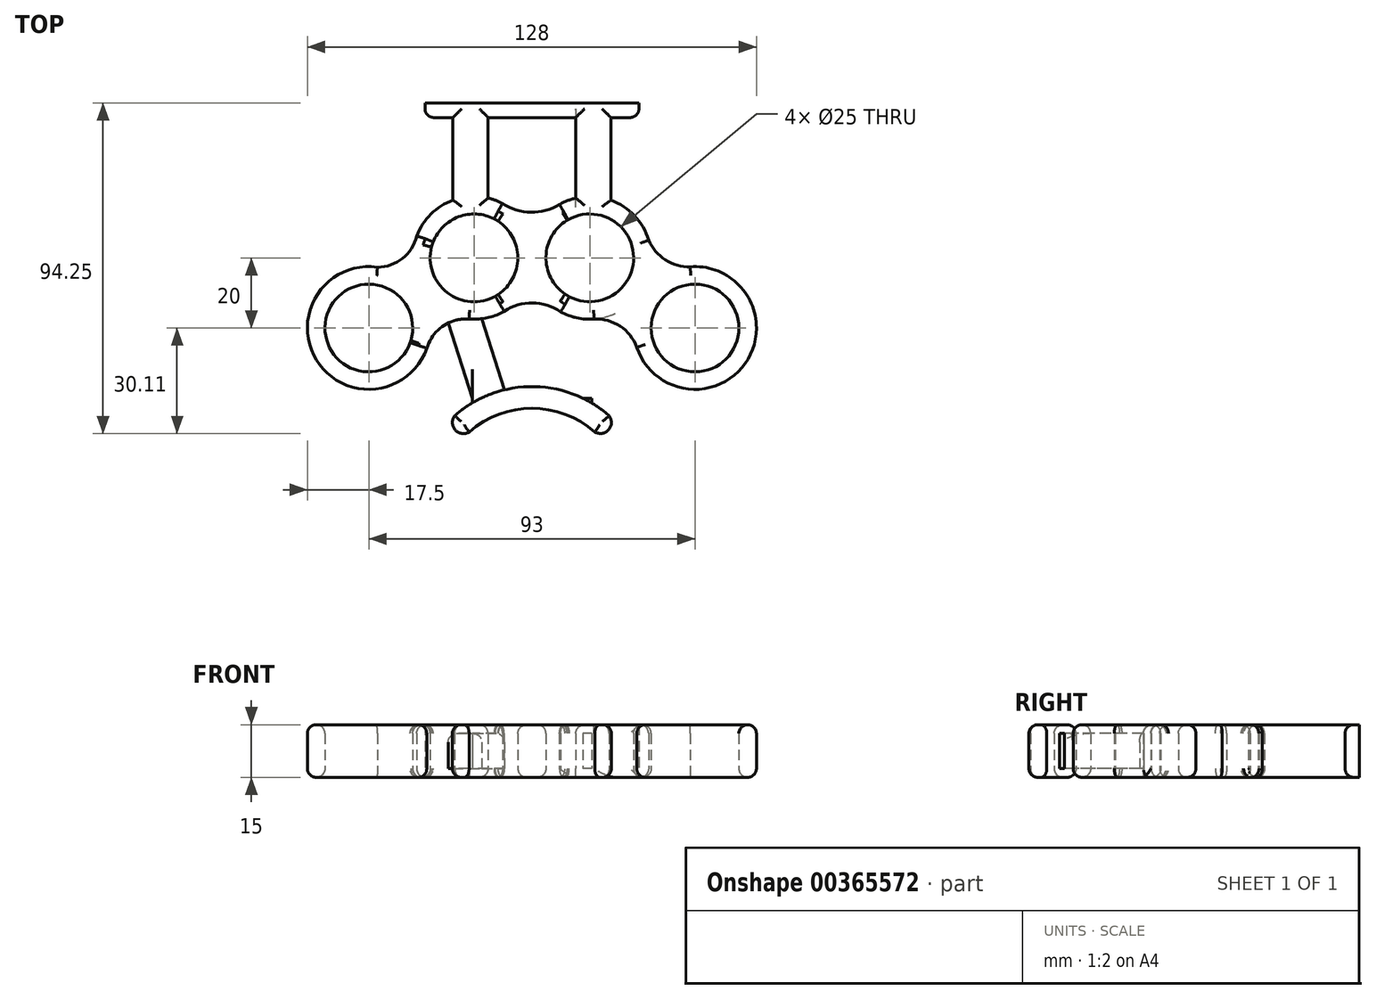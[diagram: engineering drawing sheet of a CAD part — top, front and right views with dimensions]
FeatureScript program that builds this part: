
annotation { "Feature Type Name" : "Feature", "Feature Type Description" : "" }
export const myFeature = defineFeature(function(context is Context, id is Id, definition is map)
    precondition{}
    {
        {
            var Q0;
            Q0=qCreatedBy(makeId("Top.planeOp"),FACE);
            var sketch = newSketch(context, id + "F0", { "sketchPlane" : qUnion([Q0])});
            skLineSegment(sketch, "E0", {"start": v(0, 0) * mm, "end": v(-16.5, 0) * mm});
            skLineSegment(sketch, "E1", {"start": v(0, 0) * mm, "end": v(16.5, 0) * mm});
            skCircle(sketch, "E2", {"center": v(-16.5, 0) * mm, "radius": 12.5 * mm});
            skCircle(sketch, "E3", {"center": v(16.5, 0) * mm, "radius": 12.5 * mm});
            skCircle(sketch, "E4", {"center": v(-46.5, -20) * mm, "radius": 12.5 * mm});
            skCircle(sketch, "E5", {"center": v(46.5, -20) * mm, "radius": 12.5 * mm});
            skCircle(sketch, "E6.0", {"center": v(-46.5, -20) * mm, "radius": 17.5 * mm});
            skCircle(sketch, "E7.0", {"center": v(-16.5, 0) * mm, "radius": 17.5 * mm});
            skCircle(sketch, "E8.0", {"center": v(16.5, 0) * mm, "radius": 17.5 * mm});
            skCircle(sketch, "E9.0", {"center": v(46.5, -20) * mm, "radius": 17.5 * mm});
            skArc(sketch, "E10", {"start": v(-8.38, 15.5) * mm, "mid": v(-0.3, 13.01) * mm, "end": v(7.85, 15.21) * mm});
            skArc(sketch, "E11", {"start": v(-44.04, -2.67) * mm, "mid": v(-36.9, -0.16) * mm, "end": v(-32.85, 6.23) * mm});
            skArc(sketch, "E12", {"start": v(8.17, -15.4) * mm, "mid": v(0.16, -12.86) * mm, "end": v(-7.9, -15.24) * mm});
            skArc(sketch, "E13", {"start": v(33.26, 5.03) * mm, "mid": v(38.06, -0.54) * mm, "end": v(45.14, -2.55) * mm});
            skArc(sketch, "E14", {"start": v(-17.95, -17.44) * mm, "mid": v(-25.43, -19.49) * mm, "end": v(-29.98, -25.76) * mm});
            skArc(sketch, "E15", {"start": v(29.9, -25.53) * mm, "mid": v(25.15, -19.48) * mm, "end": v(17.73, -17.46) * mm});
            skLineSegment(sketch, "E16", {"start": v(-16.5, 0) * mm, "end": v(-46.5, -20) * mm});
            skLineSegment(sketch, "E17", {"start": v(16.5, 0) * mm, "end": v(46.5, -20) * mm});
            skSolve(sketch);
        }
        {
            var Q0;
            {var subQ4=sQuery(id+"F0.wireOp",EDGE,"E7.0");var subQ5=sQuery(id+"F0.wireOp",EDGE,"E1");var subQ6=makeQuery(id+"F0.imprint","INTERSECT",VERTEX,{"derivedFrom":[subQ5,subQ4]});Q0=makeQuery(id+"F0.imprint","IMPRINT",FACE,{"disambiguationData":[TD([[makeQuery(id+"F0.imprint","IMPRINT",EDGE,{"disambiguationData":[TD([[subQ6,-1.0]])],"derivedFrom":subQ5}),1.0]])]});}
            var Q1;
            {var subQ0=sQuery(id+"F0.wireOp",EDGE,"E1");var subQ1=sQuery(id+"F0.wireOp",EDGE,"E0");var subQ2=makeQuery(id+"F0.imprint","INTERSECT",VERTEX,{"derivedFrom":[subQ1,subQ0]});Q1=makeQuery(id+"F0.imprint","IMPRINT",FACE,{"disambiguationData":[TD([[makeQuery(id+"F0.imprint","IMPRINT",EDGE,{"disambiguationData":[TD([[subQ2,-1.0]])],"derivedFrom":subQ1}),-1.0]])]});}
            var Q2;
            {var subQ0=sQuery(id+"F0.wireOp",EDGE,"E10");var subQ1=sQuery(id+"F0.wireOp",EDGE,"E7.0");var subQ2=makeQuery(id+"F0.imprint","INTERSECT",VERTEX,{"disambiguationData":[OD(1.0)],"derivedFrom":[subQ1,subQ0]});Q2=makeQuery(id+"F0.imprint","IMPRINT",FACE,{"disambiguationData":[TD([[makeQuery(id+"F0.imprint","IMPRINT",EDGE,{"disambiguationData":[TD([[subQ2,1.0]])],"derivedFrom":subQ1}),-1.0]])]});}
            var Q3;
            {var subQ5=sQuery(id+"F0.wireOp",EDGE,"E8.0");var subQ6=sQuery(id+"F0.wireOp",EDGE,"E0");var subQ7=makeQuery(id+"F0.imprint","INTERSECT",VERTEX,{"derivedFrom":[subQ6,subQ5]});Q3=makeQuery(id+"F0.imprint","IMPRINT",FACE,{"disambiguationData":[TD([[makeQuery(id+"F0.imprint","IMPRINT",EDGE,{"disambiguationData":[TD([[subQ7,-1.0]])],"derivedFrom":subQ6}),-1.0]])]});}
            var Q4;
            {var subQ4=sQuery(id+"F0.wireOp",EDGE,"E8.0");var subQ5=sQuery(id+"F0.wireOp",EDGE,"E0");var subQ6=makeQuery(id+"F0.imprint","INTERSECT",VERTEX,{"derivedFrom":[subQ5,subQ4]});Q4=makeQuery(id+"F0.imprint","IMPRINT",FACE,{"disambiguationData":[TD([[makeQuery(id+"F0.imprint","IMPRINT",EDGE,{"disambiguationData":[TD([[subQ6,-1.0]])],"derivedFrom":subQ5}),1.0]])]});}
            var Q5;
            {var subQ3=sQuery(id+"F0.wireOp",EDGE,"E7.0");var subQ5=sQuery(id+"F0.wireOp",EDGE,"E1");var subQ6=makeQuery(id+"F0.imprint","INTERSECT",VERTEX,{"derivedFrom":[subQ5,subQ3]});Q5=makeQuery(id+"F0.imprint","IMPRINT",FACE,{"disambiguationData":[TD([[makeQuery(id+"F0.imprint","IMPRINT",EDGE,{"disambiguationData":[TD([[subQ6,-1.0]])],"derivedFrom":subQ5}),-1.0]])]});}
            var Q6;
            {var subQ0=sQuery(id+"F0.wireOp",EDGE,"E1");var subQ1=sQuery(id+"F0.wireOp",EDGE,"E0");var subQ2=makeQuery(id+"F0.imprint","INTERSECT",VERTEX,{"derivedFrom":[subQ1,subQ0]});Q6=makeQuery(id+"F0.imprint","IMPRINT",FACE,{"disambiguationData":[TD([[makeQuery(id+"F0.imprint","IMPRINT",EDGE,{"disambiguationData":[TD([[subQ2,-1.0]])],"derivedFrom":subQ1}),1.0]])]});}
            var Q7;
            {var subQ0=sQuery(id+"F0.wireOp",EDGE,"E12");var subQ1=sQuery(id+"F0.wireOp",EDGE,"E7.0");var subQ2=makeQuery(id+"F0.imprint","INTERSECT",VERTEX,{"disambiguationData":[OD(1.0)],"derivedFrom":[subQ1,subQ0]});Q7=makeQuery(id+"F0.imprint","IMPRINT",FACE,{"disambiguationData":[TD([[makeQuery(id+"F0.imprint","IMPRINT",EDGE,{"disambiguationData":[TD([[subQ2,-1.0]])],"derivedFrom":subQ1}),-1.0]])]});}
            var Q8;
            {var subQ0=sQuery(id+"F0.wireOp",EDGE,"E15");Q8=makeQuery(id+"F0.imprint","IMPRINT",FACE,{"disambiguationData":[TD([[makeQuery(id+"F0.imprint","IMPRINT",EDGE,{"derivedFrom":subQ0}),-1.0]])]});}
            var Q9;
            {var subQ0=sQuery(id+"F0.wireOp",EDGE,"E13");Q9=makeQuery(id+"F0.imprint","IMPRINT",FACE,{"disambiguationData":[TD([[makeQuery(id+"F0.imprint","IMPRINT",EDGE,{"derivedFrom":subQ0}),-1.0]])]});}
            var Q10;
            Q10=makeQuery(id+"F0.imprint","IMPRINT",FACE,{"disambiguationData":[TD([[makeQuery(id+"F0.imprint","IMPRINT",EDGE,{"derivedFrom":sQuery(id+"F0.wireOp",EDGE,"E5")}),-1.0]])]});
            var Q11;
            Q11=makeQuery(id+"F0.imprint","IMPRINT",FACE,{"disambiguationData":[TD([[makeQuery(id+"F0.imprint","IMPRINT",EDGE,{"derivedFrom":sQuery(id+"F0.wireOp",EDGE,"E4")}),-1.0]])]});
            var Q12;
            {var subQ0=sQuery(id+"F0.wireOp",EDGE,"E16");var subQ1=sQuery(id+"F0.wireOp",EDGE,"E6.0");var subQ2=makeQuery(id+"F0.imprint","INTERSECT",VERTEX,{"derivedFrom":[subQ1,subQ0]});Q12=makeQuery(id+"F0.imprint","IMPRINT",FACE,{"disambiguationData":[TD([[makeQuery(id+"F0.imprint","IMPRINT",EDGE,{"disambiguationData":[TD([[subQ2,1.0]])],"derivedFrom":subQ1}),-1.0]])]});}
            var Q13;
            {var subQ0=sQuery(id+"F0.wireOp",EDGE,"E11");var subQ1=sQuery(id+"F0.wireOp",EDGE,"E6.0");var subQ2=makeQuery(id+"F0.imprint","INTERSECT",VERTEX,{"derivedFrom":[subQ1,subQ0]});Q13=makeQuery(id+"F0.imprint","IMPRINT",FACE,{"disambiguationData":[TD([[makeQuery(id+"F0.imprint","IMPRINT",EDGE,{"disambiguationData":[TD([[subQ2,1.0]])],"derivedFrom":subQ1}),-1.0]])]});}
            extrude(context, id + "F1", {"entities" : qUnion([Q0, Q1, Q2, Q3, Q4, Q5, Q6, Q7, Q8, Q9, Q10, Q11, Q12, Q13]), "depth" : 15 * mm});
        }
        {
            var Q0;
            Q0=qCreatedBy(makeId("Top.planeOp"),FACE);
            var sketch = newSketch(context, id + "F2", { "sketchPlane" : qUnion([Q0])});
            skLineSegment(sketch, "E18", {"start": v(0, 0) * mm, "end": v(0, 15) * mm});
            skLineSegment(sketch, "E19", {"start": v(0, 15) * mm, "end": v(-12.5, 15) * mm});
            skLineSegment(sketch, "E20", {"start": v(0, 15) * mm, "end": v(12.5, 15) * mm});
            skLineSegment(sketch, "E21", {"start": v(-12.5, 15) * mm, "end": v(-12.5, 40) * mm});
            skLineSegment(sketch, "E22", {"start": v(12.5, 15) * mm, "end": v(12.5, 40) * mm});
            skLineSegment(sketch, "E23", {"start": v(12.5, 15) * mm, "end": v(22.5, 15) * mm});
            skLineSegment(sketch, "E24", {"start": v(22.5, 15) * mm, "end": v(22.5, 40) * mm});
            skLineSegment(sketch, "E25", {"start": v(-12.5, 15) * mm, "end": v(-22.5, 15) * mm});
            skLineSegment(sketch, "E26", {"start": v(-22.5, 15) * mm, "end": v(-22.5, 40) * mm});
            skLineSegment(sketch, "E27", {"start": v(-22.5, 40) * mm, "end": v(-12.5, 40) * mm});
            skLineSegment(sketch, "E28", {"start": v(12.5, 40) * mm, "end": v(22.5, 40) * mm});
            skLineSegment(sketch, "E29", {"start": v(30.5, 40) * mm, "end": v(30.5, 44.14) * mm});
            skLineSegment(sketch, "E30", {"start": v(30.5, 44.14) * mm, "end": v(-30.5, 44.14) * mm});
            skLineSegment(sketch, "E31", {"start": v(-30.5, 44.14) * mm, "end": v(-30.5, 40) * mm});
            skLineSegment(sketch, "E32", {"start": v(-30.5, 40) * mm, "end": v(-22.5, 40) * mm});
            skLineSegment(sketch, "E33", {"start": v(-12.5, 40) * mm, "end": v(12.5, 40) * mm});
            skLineSegment(sketch, "E34", {"start": v(22.5, 40) * mm, "end": v(30.5, 40) * mm});
            skSolve(sketch);
        }
        {
            var Q0;
            Q0=makeQuery(id+"F2.imprint","IMPRINT",FACE,{"disambiguationData":[TD([[makeQuery(id+"F2.imprint","IMPRINT",EDGE,{"derivedFrom":sQuery(id+"F2.wireOp",EDGE,"E21")}),1.0]])]});
            var Q1;
            Q1=makeQuery(id+"F2.imprint","IMPRINT",FACE,{"disambiguationData":[TD([[makeQuery(id+"F2.imprint","IMPRINT",EDGE,{"derivedFrom":sQuery(id+"F2.wireOp",EDGE,"E22")}),-1.0]])]});
            var Q2;
            Q2=makeQuery(id+"F2.imprint","IMPRINT",FACE,{"disambiguationData":[TD([[makeQuery(id+"F2.imprint","IMPRINT",EDGE,{"derivedFrom":sQuery(id+"F2.wireOp",EDGE,"E27")}),1.0]])]});
            extrude(context, id + "F3", {"entities" : qUnion([Q0, Q1, Q2]), "operationType" : NewBodyOperationType.ADD, "depth" : 15 * mm});
        }
        {
            var Q0;
            Q0=qCreatedBy(makeId("Top.planeOp"),FACE);
            var sketch = newSketch(context, id + "F4", { "sketchPlane" : qUnion([Q0])});
            skLineSegment(sketch, "E35", {"start": v(0, 0) * mm, "end": v(0, -15) * mm});
            skLineSegment(sketch, "E36", {"start": v(0, -15) * mm, "end": v(-25, -15) * mm});
            skLineSegment(sketch, "E37", {"start": v(0, -15) * mm, "end": v(25, -15) * mm});
            skLineSegment(sketch, "E38", {"start": v(-25, -15) * mm, "end": v(-17, -40) * mm});
            skLineSegment(sketch, "E39", {"start": v(-17, -40) * mm, "end": v(-7, -40) * mm});
            skLineSegment(sketch, "E40", {"start": v(-25, -15) * mm, "end": v(-15, -15) * mm});
            skLineSegment(sketch, "E41", {"start": v(-15, -15) * mm, "end": v(-7, -40) * mm});
            skLineSegment(sketch, "E42", {"start": v(17, -40) * mm, "end": v(7, -40) * mm});
            skLineSegment(sketch, "E43", {"start": v(25, -15) * mm, "end": v(15, -15) * mm});
            skLineSegment(sketch, "E44", {"start": v(25, -15) * mm, "end": v(17, -40) * mm});
            skLineSegment(sketch, "E45", {"start": v(7, -40) * mm, "end": v(15, -15) * mm});
            skLineSegment(sketch, "E46", {"start": v(-17, -40) * mm, "end": v(-17, -45) * mm});
            skLineSegment(sketch, "E47", {"start": v(-17, -45) * mm, "end": v(-22, -45) * mm});
            skLineSegment(sketch, "E48", {"start": v(17, -40) * mm, "end": v(17, -45) * mm});
            skLineSegment(sketch, "E49", {"start": v(17, -45) * mm, "end": v(22, -45) * mm});
            skArc(sketch, "E50", {"start": v(22, -45) * mm, "mid": v(0, -36.7) * mm, "end": v(-22, -45) * mm});
            skArc(sketch, "E51.0", {"start": v(17.9, -49.65) * mm, "mid": v(0, -42.9) * mm, "end": v(-17.9, -49.65) * mm});
            skArc(sketch, "E52", {"start": v(-22, -45) * mm, "mid": v(-21.9, -49.04) * mm, "end": v(-17.9, -49.65) * mm});
            skArc(sketch, "E53", {"start": v(17.9, -49.65) * mm, "mid": v(21.86, -49.01) * mm, "end": v(22, -45) * mm});
            skSolve(sketch);
        }
        {
            var Q0;
            {var subQ5=sQuery(id+"F4.wireOp",EDGE,"E38");Q0=makeQuery(id+"F4.imprint","IMPRINT",FACE,{"disambiguationData":[TD([[makeQuery(id+"F4.imprint","IMPRINT",EDGE,{"derivedFrom":subQ5}),1.0]])]});}
            var Q1;
            {var subQ6=sQuery(id+"F4.wireOp",EDGE,"E43");Q1=makeQuery(id+"F4.imprint","IMPRINT",FACE,{"disambiguationData":[TD([[makeQuery(id+"F4.imprint","IMPRINT",EDGE,{"derivedFrom":subQ6}),1.0]])]});}
            var Q2;
            {var subQ0=sQuery(id+"F4.wireOp",EDGE,"E46");var subQ3=sQuery(id+"F4.wireOp",EDGE,"E50");var subQ5=makeQuery(id+"F4.imprint","INTERSECT",VERTEX,{"derivedFrom":[subQ0,subQ3]});Q2=makeQuery(id+"F4.imprint","IMPRINT",FACE,{"disambiguationData":[TD([[makeQuery(id+"F4.imprint","IMPRINT",EDGE,{"disambiguationData":[TD([[subQ5,1.0]])],"derivedFrom":subQ3}),-1.0]])]});}
            var Q3;
            {var subQ0=sQuery(id+"F4.wireOp",EDGE,"E48");var subQ3=sQuery(id+"F4.wireOp",EDGE,"E50");var subQ5=makeQuery(id+"F4.imprint","INTERSECT",VERTEX,{"derivedFrom":[subQ0,subQ3]});Q3=makeQuery(id+"F4.imprint","IMPRINT",FACE,{"disambiguationData":[TD([[makeQuery(id+"F4.imprint","IMPRINT",EDGE,{"disambiguationData":[TD([[subQ5,-1.0]])],"derivedFrom":subQ3}),-1.0]])]});}
            extrude(context, id + "F5", {"entities" : qUnion([Q0, Q1, Q2, Q3]), "operationType" : NewBodyOperationType.ADD, "depth" : 12.5 * mm});
        }
        {
            var Q0;
            {var subQ5=sQuery(id+"F4.wireOp",EDGE,"E38");Q0=makeQuery(id+"F4.imprint","IMPRINT",FACE,{"disambiguationData":[TD([[makeQuery(id+"F4.imprint","IMPRINT",EDGE,{"derivedFrom":subQ5}),1.0]])]});}
            var Q1;
            {var subQ6=sQuery(id+"F4.wireOp",EDGE,"E43");Q1=makeQuery(id+"F4.imprint","IMPRINT",FACE,{"disambiguationData":[TD([[makeQuery(id+"F4.imprint","IMPRINT",EDGE,{"derivedFrom":subQ6}),1.0]])]});}
            var Q2;
            {var subQ0=sQuery(id+"F4.wireOp",EDGE,"E46");var subQ3=sQuery(id+"F4.wireOp",EDGE,"E50");var subQ5=makeQuery(id+"F4.imprint","INTERSECT",VERTEX,{"derivedFrom":[subQ0,subQ3]});Q2=makeQuery(id+"F4.imprint","IMPRINT",FACE,{"disambiguationData":[TD([[makeQuery(id+"F4.imprint","IMPRINT",EDGE,{"disambiguationData":[TD([[subQ5,1.0]])],"derivedFrom":subQ3}),-1.0]])]});}
            var Q3;
            {var subQ0=sQuery(id+"F4.wireOp",EDGE,"E48");var subQ3=sQuery(id+"F4.wireOp",EDGE,"E50");var subQ5=makeQuery(id+"F4.imprint","INTERSECT",VERTEX,{"derivedFrom":[subQ0,subQ3]});Q3=makeQuery(id+"F4.imprint","IMPRINT",FACE,{"disambiguationData":[TD([[makeQuery(id+"F4.imprint","IMPRINT",EDGE,{"disambiguationData":[TD([[subQ5,-1.0]])],"derivedFrom":subQ3}),-1.0]])]});}
            extrude(context, id + "F6", {"entities" : qUnion([Q0, Q1, Q2, Q3]), "operationType" : NewBodyOperationType.REMOVE, "depth" : 2.5 * mm});
        }
        {
            var Q0;
            Q0=makeQuery(id+"F3.boolean.opBoolean","MERGE",FACE,{"derivedFrom":[makeQuery(id+"F1.opExtrude","CAP_FACE",FACE,{"disambiguationData":[OSD([sQuery(id+"F0.wireOp",EDGE,"E2"),sQuery(id+"F0.wireOp",EDGE,"E3"),sQuery(id+"F0.wireOp",EDGE,"E4"),sQuery(id+"F0.wireOp",EDGE,"E5"),sQuery(id+"F0.wireOp",EDGE,"E6.0"),sQuery(id+"F0.wireOp",EDGE,"E7.0"),sQuery(id+"F0.wireOp",EDGE,"E8.0"),sQuery(id+"F0.wireOp",EDGE,"E9.0"),sQuery(id+"F0.wireOp",EDGE,"E10"),sQuery(id+"F0.wireOp",EDGE,"E11"),sQuery(id+"F0.wireOp",EDGE,"E12"),sQuery(id+"F0.wireOp",EDGE,"E13"),sQuery(id+"F0.wireOp",EDGE,"E14"),sQuery(id+"F0.wireOp",EDGE,"E15")])],"isStart":false}),makeQuery(id+"F3.opExtrude","CAP_FACE",FACE,{"disambiguationData":[OSD([sQuery(id+"F2.wireOp",EDGE,"E21"),sQuery(id+"F2.wireOp",EDGE,"E22"),sQuery(id+"F2.wireOp",EDGE,"E23"),sQuery(id+"F2.wireOp",EDGE,"E24"),sQuery(id+"F2.wireOp",EDGE,"E25"),sQuery(id+"F2.wireOp",EDGE,"E26"),sQuery(id+"F2.wireOp",EDGE,"E29"),sQuery(id+"F2.wireOp",EDGE,"E30"),sQuery(id+"F2.wireOp",EDGE,"E31"),sQuery(id+"F2.wireOp",EDGE,"E32"),sQuery(id+"F2.wireOp",EDGE,"E33"),sQuery(id+"F2.wireOp",EDGE,"E34")])],"isStart":false})]});
            extrude(context, id + "F7", {"entities" : qUnion([Q0]), "operationType" : NewBodyOperationType.ADD, "oppositeDirection" : true, "depth" : 15 * mm});
        }
        {
            var Q0;
            {var subQ6=sQuery(id+"F4.wireOp",EDGE,"E47");Q0=makeQuery(id+"F4.imprint","IMPRINT",FACE,{"disambiguationData":[TD([[makeQuery(id+"F4.imprint","IMPRINT",EDGE,{"derivedFrom":subQ6}),1.0]])]});}
            var Q1;
            {var subQ0=sQuery(id+"F4.wireOp",EDGE,"E45");var subQ1=sQuery(id+"F4.wireOp",EDGE,"E42");var subQ2=makeQuery(id+"F4.imprint","INTERSECT",VERTEX,{"derivedFrom":[subQ1,subQ0]});Q1=makeQuery(id+"F4.imprint","IMPRINT",FACE,{"disambiguationData":[TD([[makeQuery(id+"F4.imprint","IMPRINT",EDGE,{"disambiguationData":[TD([[subQ2,1.0]])],"derivedFrom":subQ1}),-1.0]])]});}
            var Q2;
            {var subQ0=sQuery(id+"F4.wireOp",EDGE,"E41");var subQ1=sQuery(id+"F4.wireOp",EDGE,"E39");var subQ2=makeQuery(id+"F4.imprint","INTERSECT",VERTEX,{"derivedFrom":[subQ1,subQ0]});Q2=makeQuery(id+"F4.imprint","IMPRINT",FACE,{"disambiguationData":[TD([[makeQuery(id+"F4.imprint","IMPRINT",EDGE,{"disambiguationData":[TD([[subQ2,1.0]])],"derivedFrom":subQ1}),1.0]])]});}
            var Q3;
            {var subQ0=sQuery(id+"F4.wireOp",EDGE,"E47");Q3=makeQuery(id+"F4.imprint","IMPRINT",FACE,{"disambiguationData":[TD([[makeQuery(id+"F4.imprint","IMPRINT",EDGE,{"derivedFrom":subQ0}),-1.0]])]});}
            var Q4;
            {var subQ0=sQuery(id+"F4.wireOp",EDGE,"E49");Q4=makeQuery(id+"F4.imprint","IMPRINT",FACE,{"disambiguationData":[TD([[makeQuery(id+"F4.imprint","IMPRINT",EDGE,{"derivedFrom":subQ0}),1.0]])]});}
            extrude(context, id + "F8", {"entities" : qUnion([Q0, Q1, Q2, Q3, Q4]), "operationType" : NewBodyOperationType.ADD, "depth" : 15 * mm});
        }
        {
            var Q0;
            Q0=makeQuery(id+"F1.opExtrude","CAP_EDGE",EDGE,{"disambiguationData":[OSD([sQuery(id+"F0.wireOp",EDGE,"E9.0")])],"isStart":false});
            var Q1;
            {var subQ1=sQuery(id+"F0.wireOp",EDGE,"E13");var subQ2=sQuery(id+"F0.wireOp",EDGE,"E10");var subQ3=sQuery(id+"F0.wireOp",EDGE,"E8.0");var subQ4=makeQuery(id+"F0.imprint","IMPRINT",EDGE,{"disambiguationData":[TD([[makeQuery(id+"F0.imprint","INTERSECT",VERTEX,{"disambiguationData":[OD(0.0)],"derivedFrom":[subQ3,subQ2]}),1.0]])],"derivedFrom":subQ3});Q1=makeQuery(id+"F3.boolean.opBoolean","SPLIT",EDGE,{"disambiguationData":[TD([makeQuery(id+"F1.opExtrude","SWEPT_FACE",FACE,{"disambiguationData":[OSD([subQ1])]})])],"derivedFrom":makeQuery(id+"F1.opExtrude","CAP_EDGE",EDGE,{"disambiguationData":[OSD([subQ3]),TDD([subQ4])],"isStart":false})});}
            var Q2;
            {var subQ0=sQuery(id+"F0.wireOp",EDGE,"E8.0");Q2=makeQuery(id+"F1.opExtrude","CAP_EDGE",EDGE,{"disambiguationData":[OSD([subQ0]),TDD([makeQuery(id+"F0.imprint","IMPRINT",EDGE,{"disambiguationData":[TD([[makeQuery(id+"F0.imprint","INTERSECT",VERTEX,{"disambiguationData":[OD(0.0)],"derivedFrom":[subQ0,sQuery(id+"F0.wireOp",EDGE,"E12")]}),-1.0]])],"derivedFrom":subQ0})])],"isStart":false});}
            var Q3;
            Q3=makeQuery(id+"F1.opExtrude","CAP_EDGE",EDGE,{"disambiguationData":[OSD([sQuery(id+"F0.wireOp",EDGE,"E6.0")])],"isStart":false});
            var Q4;
            {var subQ0=sQuery(id+"F0.wireOp",EDGE,"E7.0");Q4=makeQuery(id+"F1.opExtrude","CAP_EDGE",EDGE,{"disambiguationData":[OSD([subQ0]),TDD([makeQuery(id+"F0.imprint","IMPRINT",EDGE,{"disambiguationData":[TD([[makeQuery(id+"F0.imprint","INTERSECT",VERTEX,{"disambiguationData":[OD(0.0)],"derivedFrom":[subQ0,sQuery(id+"F0.wireOp",EDGE,"E12")]}),1.0]])],"derivedFrom":subQ0})])],"isStart":false});}
            var Q5;
            Q5=makeQuery(id+"F1.opExtrude","CAP_EDGE",EDGE,{"disambiguationData":[OSD([sQuery(id+"F0.wireOp",EDGE,"E14")])],"isStart":false});
            var Q6;
            Q6=makeQuery(id+"F1.opExtrude","CAP_EDGE",EDGE,{"disambiguationData":[OSD([sQuery(id+"F0.wireOp",EDGE,"E12")])],"isStart":false});
            var Q7;
            Q7=makeQuery(id+"F1.opExtrude","CAP_EDGE",EDGE,{"disambiguationData":[OSD([sQuery(id+"F0.wireOp",EDGE,"E15")])],"isStart":false});
            var Q8;
            Q8=makeQuery(id+"F1.opExtrude","CAP_EDGE",EDGE,{"disambiguationData":[OSD([sQuery(id+"F0.wireOp",EDGE,"E13")])],"isStart":false});
            var Q9;
            Q9=makeQuery(id+"F3.opExtrude","CAP_EDGE",EDGE,{"disambiguationData":[OSD([sQuery(id+"F2.wireOp",EDGE,"E24")])],"isStart":false});
            var Q10;
            Q10=makeQuery(id+"F3.opExtrude","CAP_EDGE",EDGE,{"disambiguationData":[OSD([sQuery(id+"F2.wireOp",EDGE,"E22")])],"isStart":false});
            var Q11;
            Q11=makeQuery(id+"F1.opExtrude","CAP_EDGE",EDGE,{"disambiguationData":[OSD([sQuery(id+"F0.wireOp",EDGE,"E10")])],"isStart":false});
            var Q12;
            {var subQ1=sQuery(id+"F0.wireOp",EDGE,"E10");var subQ2=sQuery(id+"F0.wireOp",EDGE,"E8.0");var subQ4=makeQuery(id+"F0.imprint","IMPRINT",EDGE,{"disambiguationData":[TD([[makeQuery(id+"F0.imprint","INTERSECT",VERTEX,{"disambiguationData":[OD(0.0)],"derivedFrom":[subQ2,subQ1]}),1.0]])],"derivedFrom":subQ2});Q12=makeQuery(id+"F3.boolean.opBoolean","SPLIT",EDGE,{"disambiguationData":[TD([makeQuery(id+"F1.opExtrude","SWEPT_FACE",FACE,{"disambiguationData":[OSD([subQ1])]})])],"derivedFrom":makeQuery(id+"F1.opExtrude","CAP_EDGE",EDGE,{"disambiguationData":[OSD([subQ2]),TDD([subQ4])],"isStart":false})});}
            var Q13;
            {var subQ1=sQuery(id+"F0.wireOp",EDGE,"E10");var subQ2=sQuery(id+"F0.wireOp",EDGE,"E7.0");var subQ4=makeQuery(id+"F0.imprint","IMPRINT",EDGE,{"disambiguationData":[TD([[makeQuery(id+"F0.imprint","INTERSECT",VERTEX,{"disambiguationData":[OD(0.0)],"derivedFrom":[subQ2,subQ1]}),-1.0]])],"derivedFrom":subQ2});Q13=makeQuery(id+"F3.boolean.opBoolean","SPLIT",EDGE,{"disambiguationData":[TD([makeQuery(id+"F1.opExtrude","SWEPT_FACE",FACE,{"disambiguationData":[OSD([subQ1])]})])],"derivedFrom":makeQuery(id+"F1.opExtrude","CAP_EDGE",EDGE,{"disambiguationData":[OSD([subQ2]),TDD([subQ4])],"isStart":false})});}
            var Q14;
            {var subQ1=sQuery(id+"F0.wireOp",EDGE,"E11");var subQ2=sQuery(id+"F0.wireOp",EDGE,"E10");var subQ3=sQuery(id+"F0.wireOp",EDGE,"E7.0");var subQ4=makeQuery(id+"F0.imprint","IMPRINT",EDGE,{"disambiguationData":[TD([[makeQuery(id+"F0.imprint","INTERSECT",VERTEX,{"disambiguationData":[OD(0.0)],"derivedFrom":[subQ3,subQ2]}),-1.0]])],"derivedFrom":subQ3});Q14=makeQuery(id+"F3.boolean.opBoolean","SPLIT",EDGE,{"disambiguationData":[TD([makeQuery(id+"F1.opExtrude","SWEPT_FACE",FACE,{"disambiguationData":[OSD([subQ1])]})])],"derivedFrom":makeQuery(id+"F1.opExtrude","CAP_EDGE",EDGE,{"disambiguationData":[OSD([subQ3]),TDD([subQ4])],"isStart":false})});}
            var Q15;
            Q15=makeQuery(id+"F1.opExtrude","CAP_EDGE",EDGE,{"disambiguationData":[OSD([sQuery(id+"F0.wireOp",EDGE,"E11")])],"isStart":false});
            var Q16;
            Q16=makeQuery(id+"F3.opExtrude","CAP_EDGE",EDGE,{"disambiguationData":[OSD([sQuery(id+"F2.wireOp",EDGE,"E26")])],"isStart":false});
            var Q17;
            Q17=makeQuery(id+"F3.opExtrude","CAP_EDGE",EDGE,{"disambiguationData":[OSD([sQuery(id+"F2.wireOp",EDGE,"E21")])],"isStart":false});
            var Q18;
            Q18=makeQuery(id+"F3.opExtrude","CAP_EDGE",EDGE,{"disambiguationData":[OSD([sQuery(id+"F2.wireOp",EDGE,"E33")])],"isStart":false});
            var Q19;
            Q19=makeQuery(id+"F3.opExtrude","SWEPT_EDGE",EDGE,{"disambiguationData":[OSD([sQuery(id+"F2.wireOp",EDGE,"E29"),sQuery(id+"F2.wireOp",EDGE,"E34")])]});
            var Q20;
            Q20=makeQuery(id+"F3.opExtrude","CAP_EDGE",EDGE,{"disambiguationData":[OSD([sQuery(id+"F2.wireOp",EDGE,"E32")])],"isStart":false});
            var Q21;
            Q21=makeQuery(id+"F3.opExtrude","SWEPT_EDGE",EDGE,{"disambiguationData":[OSD([sQuery(id+"F2.wireOp",EDGE,"E31"),sQuery(id+"F2.wireOp",EDGE,"E32")])]});
            var Q22;
            Q22=makeQuery(id+"F3.opExtrude","CAP_EDGE",EDGE,{"disambiguationData":[OSD([sQuery(id+"F2.wireOp",EDGE,"E32")])],"isStart":true});
            var Q23;
            Q23=makeQuery(id+"F3.opExtrude","CAP_EDGE",EDGE,{"disambiguationData":[OSD([sQuery(id+"F2.wireOp",EDGE,"E34")])],"isStart":true});
            var Q24;
            Q24=makeQuery(id+"F3.opExtrude","CAP_EDGE",EDGE,{"disambiguationData":[OSD([sQuery(id+"F2.wireOp",EDGE,"E24")])],"isStart":true});
            var Q25;
            Q25=makeQuery(id+"F3.opExtrude","CAP_EDGE",EDGE,{"disambiguationData":[OSD([sQuery(id+"F2.wireOp",EDGE,"E33")])],"isStart":true});
            var Q26;
            Q26=makeQuery(id+"F3.opExtrude","CAP_EDGE",EDGE,{"disambiguationData":[OSD([sQuery(id+"F2.wireOp",EDGE,"E21")])],"isStart":true});
            var Q27;
            Q27=makeQuery(id+"F3.opExtrude","CAP_EDGE",EDGE,{"disambiguationData":[OSD([sQuery(id+"F2.wireOp",EDGE,"E26")])],"isStart":true});
            var Q28;
            {var subQ1=sQuery(id+"F0.wireOp",EDGE,"E10");var subQ3=sQuery(id+"F0.wireOp",EDGE,"E7.0");var subQ4=makeQuery(id+"F0.imprint","IMPRINT",EDGE,{"disambiguationData":[TD([[makeQuery(id+"F0.imprint","INTERSECT",VERTEX,{"disambiguationData":[OD(0.0)],"derivedFrom":[subQ3,subQ1]}),-1.0]])],"derivedFrom":subQ3});Q28=makeQuery(id+"F3.boolean.opBoolean","SPLIT",EDGE,{"disambiguationData":[TD([makeQuery(id+"F1.opExtrude","SWEPT_FACE",FACE,{"disambiguationData":[OSD([subQ1])]})])],"derivedFrom":makeQuery(id+"F1.opExtrude","CAP_EDGE",EDGE,{"disambiguationData":[OSD([subQ3]),TDD([subQ4])],"isStart":true})});}
            var Q29;
            Q29=makeQuery(id+"F1.opExtrude","CAP_EDGE",EDGE,{"disambiguationData":[OSD([sQuery(id+"F0.wireOp",EDGE,"E10")])],"isStart":true});
            var Q30;
            {var subQ0=sQuery(id+"F0.wireOp",EDGE,"E10");var subQ2=sQuery(id+"F0.wireOp",EDGE,"E8.0");var subQ4=makeQuery(id+"F0.imprint","IMPRINT",EDGE,{"disambiguationData":[TD([[makeQuery(id+"F0.imprint","INTERSECT",VERTEX,{"disambiguationData":[OD(0.0)],"derivedFrom":[subQ2,subQ0]}),1.0]])],"derivedFrom":subQ2});Q30=makeQuery(id+"F3.boolean.opBoolean","SPLIT",EDGE,{"disambiguationData":[TD([makeQuery(id+"F1.opExtrude","SWEPT_FACE",FACE,{"disambiguationData":[OSD([subQ0])]})])],"derivedFrom":makeQuery(id+"F1.opExtrude","CAP_EDGE",EDGE,{"disambiguationData":[OSD([subQ2]),TDD([subQ4])],"isStart":true})});}
            var Q31;
            {var subQ0=sQuery(id+"F0.wireOp",EDGE,"E13");var subQ2=sQuery(id+"F0.wireOp",EDGE,"E10");var subQ3=sQuery(id+"F0.wireOp",EDGE,"E8.0");var subQ4=makeQuery(id+"F0.imprint","IMPRINT",EDGE,{"disambiguationData":[TD([[makeQuery(id+"F0.imprint","INTERSECT",VERTEX,{"disambiguationData":[OD(0.0)],"derivedFrom":[subQ3,subQ2]}),1.0]])],"derivedFrom":subQ3});Q31=makeQuery(id+"F3.boolean.opBoolean","SPLIT",EDGE,{"disambiguationData":[TD([makeQuery(id+"F1.opExtrude","SWEPT_FACE",FACE,{"disambiguationData":[OSD([subQ0])]})])],"derivedFrom":makeQuery(id+"F1.opExtrude","CAP_EDGE",EDGE,{"disambiguationData":[OSD([subQ3]),TDD([subQ4])],"isStart":true})});}
            var Q32;
            Q32=makeQuery(id+"F1.opExtrude","CAP_EDGE",EDGE,{"disambiguationData":[OSD([sQuery(id+"F0.wireOp",EDGE,"E13")])],"isStart":true});
            var Q33;
            Q33=makeQuery(id+"F1.opExtrude","CAP_EDGE",EDGE,{"disambiguationData":[OSD([sQuery(id+"F0.wireOp",EDGE,"E9.0")])],"isStart":true});
            var Q34;
            {var subQ0=sQuery(id+"F0.wireOp",EDGE,"E15");Q34=makeQuery(id+"F7.boolean.opBoolean","MERGE",EDGE,{"derivedFrom":[makeQuery(id+"F1.opExtrude","CAP_EDGE",EDGE,{"disambiguationData":[OSD([subQ0])],"isStart":true}),makeQuery(id+"F7.opExtrude","CAP_EDGE",EDGE,{"disambiguationData":[OSD([subQ0])],"isStart":false})]});}
            var Q35;
            {var subQ0=sQuery(id+"F0.wireOp",EDGE,"E8.0");var subQ1=makeQuery(id+"F0.imprint","IMPRINT",EDGE,{"disambiguationData":[TD([[makeQuery(id+"F0.imprint","INTERSECT",VERTEX,{"disambiguationData":[OD(0.0)],"derivedFrom":[subQ0,sQuery(id+"F0.wireOp",EDGE,"E12")]}),-1.0]])],"derivedFrom":subQ0});Q35=makeQuery(id+"F7.boolean.opBoolean","MERGE",EDGE,{"derivedFrom":[makeQuery(id+"F1.opExtrude","CAP_EDGE",EDGE,{"disambiguationData":[OSD([subQ0]),TDD([subQ1])],"isStart":true}),makeQuery(id+"F7.opExtrude","CAP_EDGE",EDGE,{"disambiguationData":[OSD([subQ0]),TDD([makeQuery(id+"F1.opExtrude","CAP_EDGE",EDGE,{"disambiguationData":[OSD([subQ0]),TDD([subQ1])],"isStart":false})])],"isStart":false})]});}
            var Q36;
            Q36=makeQuery(id+"F1.opExtrude","CAP_EDGE",EDGE,{"disambiguationData":[OSD([sQuery(id+"F0.wireOp",EDGE,"E12")])],"isStart":true});
            var Q37;
            {var subQ0=sQuery(id+"F0.wireOp",EDGE,"E7.0");var subQ1=makeQuery(id+"F0.imprint","IMPRINT",EDGE,{"disambiguationData":[TD([[makeQuery(id+"F0.imprint","INTERSECT",VERTEX,{"disambiguationData":[OD(0.0)],"derivedFrom":[subQ0,sQuery(id+"F0.wireOp",EDGE,"E12")]}),1.0]])],"derivedFrom":subQ0});Q37=makeQuery(id+"F7.boolean.opBoolean","MERGE",EDGE,{"derivedFrom":[makeQuery(id+"F1.opExtrude","CAP_EDGE",EDGE,{"disambiguationData":[OSD([subQ0]),TDD([subQ1])],"isStart":true}),makeQuery(id+"F7.opExtrude","CAP_EDGE",EDGE,{"disambiguationData":[OSD([subQ0]),TDD([makeQuery(id+"F1.opExtrude","CAP_EDGE",EDGE,{"disambiguationData":[OSD([subQ0]),TDD([subQ1])],"isStart":false})])],"isStart":false})]});}
            var Q38;
            {var subQ0=sQuery(id+"F0.wireOp",EDGE,"E14");Q38=makeQuery(id+"F7.boolean.opBoolean","MERGE",EDGE,{"derivedFrom":[makeQuery(id+"F1.opExtrude","CAP_EDGE",EDGE,{"disambiguationData":[OSD([subQ0])],"isStart":true}),makeQuery(id+"F7.opExtrude","CAP_EDGE",EDGE,{"disambiguationData":[OSD([subQ0])],"isStart":false})]});}
            var Q39;
            Q39=makeQuery(id+"F1.opExtrude","CAP_EDGE",EDGE,{"disambiguationData":[OSD([sQuery(id+"F0.wireOp",EDGE,"E6.0")])],"isStart":true});
            var Q40;
            Q40=makeQuery(id+"F1.opExtrude","CAP_EDGE",EDGE,{"disambiguationData":[OSD([sQuery(id+"F0.wireOp",EDGE,"E11")])],"isStart":true});
            var Q41;
            {var subQ1=sQuery(id+"F0.wireOp",EDGE,"E11");var subQ2=sQuery(id+"F0.wireOp",EDGE,"E10");var subQ3=sQuery(id+"F0.wireOp",EDGE,"E7.0");var subQ4=makeQuery(id+"F0.imprint","IMPRINT",EDGE,{"disambiguationData":[TD([[makeQuery(id+"F0.imprint","INTERSECT",VERTEX,{"disambiguationData":[OD(0.0)],"derivedFrom":[subQ3,subQ2]}),-1.0]])],"derivedFrom":subQ3});Q41=makeQuery(id+"F3.boolean.opBoolean","SPLIT",EDGE,{"disambiguationData":[TD([makeQuery(id+"F1.opExtrude","SWEPT_FACE",FACE,{"disambiguationData":[OSD([subQ1])]})])],"derivedFrom":makeQuery(id+"F1.opExtrude","CAP_EDGE",EDGE,{"disambiguationData":[OSD([subQ3]),TDD([subQ4])],"isStart":true})});}
            var Q42;
            Q42=makeQuery(id+"F3.opExtrude","CAP_EDGE",EDGE,{"disambiguationData":[OSD([sQuery(id+"F2.wireOp",EDGE,"E34")])],"isStart":false});
            fillet(context, id + "F9", {"entities" : qUnion([Q0, Q1, Q2, Q3, Q4, Q5, Q6, Q7, Q8, Q9, Q10, Q11, Q12, Q13, Q14, Q15, Q16, Q17, Q18, Q19, Q20, Q21, Q22, Q23, Q24, Q25, Q26, Q27, Q28, Q29, Q30, Q31, Q32, Q33, Q34, Q35, Q36, Q37, Q38, Q39, Q40, Q41, Q42]), "radius" : 2.5 * mm, "tangentPropagation" : true, "allowEdgeOverflow" : false});
        }
        {
            var Q0;
            Q0=makeQuery(id+"F1.opExtrude","CAP_EDGE",EDGE,{"disambiguationData":[OSD([sQuery(id+"F0.wireOp",EDGE,"E3")])],"isStart":false});
            var Q1;
            Q1=makeQuery(id+"F1.opExtrude","CAP_EDGE",EDGE,{"disambiguationData":[OSD([sQuery(id+"F0.wireOp",EDGE,"E2")])],"isStart":false});
            var Q2;
            Q2=makeQuery(id+"F1.opExtrude","CAP_EDGE",EDGE,{"disambiguationData":[OSD([sQuery(id+"F0.wireOp",EDGE,"E5")])],"isStart":false});
            var Q3;
            Q3=makeQuery(id+"F1.opExtrude","CAP_EDGE",EDGE,{"disambiguationData":[OSD([sQuery(id+"F0.wireOp",EDGE,"E4")])],"isStart":false});
            var Q4;
            Q4=makeQuery(id+"F1.opExtrude","CAP_EDGE",EDGE,{"disambiguationData":[OSD([sQuery(id+"F0.wireOp",EDGE,"E4")])],"isStart":true});
            var Q5;
            Q5=makeQuery(id+"F1.opExtrude","CAP_EDGE",EDGE,{"disambiguationData":[OSD([sQuery(id+"F0.wireOp",EDGE,"E5")])],"isStart":true});
            fillet(context, id + "F10", {"entities" : qUnion([Q0, Q1, Q2, Q3, Q4, Q5]), "radius" : 2.5 * mm, "tangentPropagation" : true, "allowEdgeOverflow" : false});
        }
        {
            var Q0;
            Q0=makeQuery(id+"F1.opExtrude","CAP_EDGE",EDGE,{"disambiguationData":[OSD([sQuery(id+"F0.wireOp",EDGE,"E2")])],"isStart":true});
            var Q1;
            Q1=makeQuery(id+"F1.opExtrude","CAP_EDGE",EDGE,{"disambiguationData":[OSD([sQuery(id+"F0.wireOp",EDGE,"E3")])],"isStart":true});
            fillet(context, id + "F11", {"entities" : qUnion([Q0, Q1]), "radius" : 2.5 * mm, "tangentPropagation" : true, "allowEdgeOverflow" : false});
        }
        {
            var Q0;
            {var subQ0=sQuery(id+"F4.wireOp",EDGE,"E38");Q0=makeQuery(id+"F6.boolean.opBoolean","COPY",EDGE,{"disambiguationData":[topologyDisambiguationEdgeConnected([makeQuery(id+"F5.opExtrude","SWEPT_FACE",FACE,{"disambiguationData":[OSD([subQ0])]})])],"derivedFrom":makeQuery(id+"F6.opExtrude","CAP_EDGE",EDGE,{"disambiguationData":[OSD([subQ0])],"isStart":false})});}
            var Q1;
            {var subQ0=sQuery(id+"F4.wireOp",EDGE,"E41");Q1=makeQuery(id+"F6.boolean.opBoolean","COPY",EDGE,{"disambiguationData":[topologyDisambiguationEdgeConnected([makeQuery(id+"F5.opExtrude","SWEPT_FACE",FACE,{"disambiguationData":[OSD([subQ0])]})])],"derivedFrom":makeQuery(id+"F6.opExtrude","CAP_EDGE",EDGE,{"disambiguationData":[OSD([subQ0])],"isStart":false})});}
            var Q2;
            {var subQ0=sQuery(id+"F4.wireOp",EDGE,"E45");Q2=makeQuery(id+"F6.boolean.opBoolean","COPY",EDGE,{"disambiguationData":[topologyDisambiguationEdgeConnected([makeQuery(id+"F5.opExtrude","SWEPT_FACE",FACE,{"disambiguationData":[OSD([subQ0])]})])],"derivedFrom":makeQuery(id+"F6.opExtrude","CAP_EDGE",EDGE,{"disambiguationData":[OSD([subQ0])],"isStart":false})});}
            var Q3;
            {var subQ0=sQuery(id+"F4.wireOp",EDGE,"E44");Q3=makeQuery(id+"F6.boolean.opBoolean","COPY",EDGE,{"disambiguationData":[topologyDisambiguationEdgeConnected([makeQuery(id+"F5.opExtrude","SWEPT_FACE",FACE,{"disambiguationData":[OSD([subQ0])]})])],"derivedFrom":makeQuery(id+"F6.opExtrude","CAP_EDGE",EDGE,{"disambiguationData":[OSD([subQ0])],"isStart":false})});}
            var Q4;
            Q4=makeQuery(id+"F5.opExtrude","CAP_EDGE",EDGE,{"disambiguationData":[OSD([sQuery(id+"F4.wireOp",EDGE,"E44")])],"isStart":false});
            var Q5;
            Q5=makeQuery(id+"F5.opExtrude","CAP_EDGE",EDGE,{"disambiguationData":[OSD([sQuery(id+"F4.wireOp",EDGE,"E45")])],"isStart":false});
            var Q6;
            Q6=makeQuery(id+"F5.opExtrude","CAP_EDGE",EDGE,{"disambiguationData":[OSD([sQuery(id+"F4.wireOp",EDGE,"E38")])],"isStart":false});
            var Q7;
            Q7=makeQuery(id+"F5.opExtrude","CAP_EDGE",EDGE,{"disambiguationData":[OSD([sQuery(id+"F4.wireOp",EDGE,"E41")])],"isStart":false});
            fillet(context, id + "F12", {"entities" : qUnion([Q0, Q1, Q2, Q3, Q4, Q5, Q6, Q7]), "radius" : 2.5 * mm, "tangentPropagation" : true, "allowEdgeOverflow" : false});
        }
        {
            var Q0;
            Q0=makeQuery(id+"F8.opExtrude","CAP_EDGE",EDGE,{"disambiguationData":[OSD([sQuery(id+"F4.wireOp",EDGE,"E51.0")])],"isStart":true});
            var Q1;
            Q1=makeQuery(id+"F8.opExtrude","CAP_EDGE",EDGE,{"disambiguationData":[OSD([sQuery(id+"F4.wireOp",EDGE,"E50")])],"isStart":true});
            var Q2;
            Q2=makeQuery(id+"F8.opExtrude","CAP_EDGE",EDGE,{"disambiguationData":[OSD([sQuery(id+"F4.wireOp",EDGE,"E53")])],"isStart":true});
            var Q3;
            Q3=makeQuery(id+"F8.opExtrude","CAP_EDGE",EDGE,{"disambiguationData":[OSD([sQuery(id+"F4.wireOp",EDGE,"E52")])],"isStart":true});
            var Q4;
            Q4=makeQuery(id+"F8.opExtrude","CAP_FACE",FACE,{"disambiguationData":[OSD([sQuery(id+"F4.wireOp",EDGE,"E50"),sQuery(id+"F4.wireOp",EDGE,"E51.0"),sQuery(id+"F4.wireOp",EDGE,"E52"),sQuery(id+"F4.wireOp",EDGE,"E53")])],"isStart":false});
            fillet(context, id + "F13", {"entities" : qUnion([Q0, Q1, Q2, Q3, Q4]), "radius" : 2.5 * mm, "tangentPropagation" : true, "allowEdgeOverflow" : false});
        }
    });
